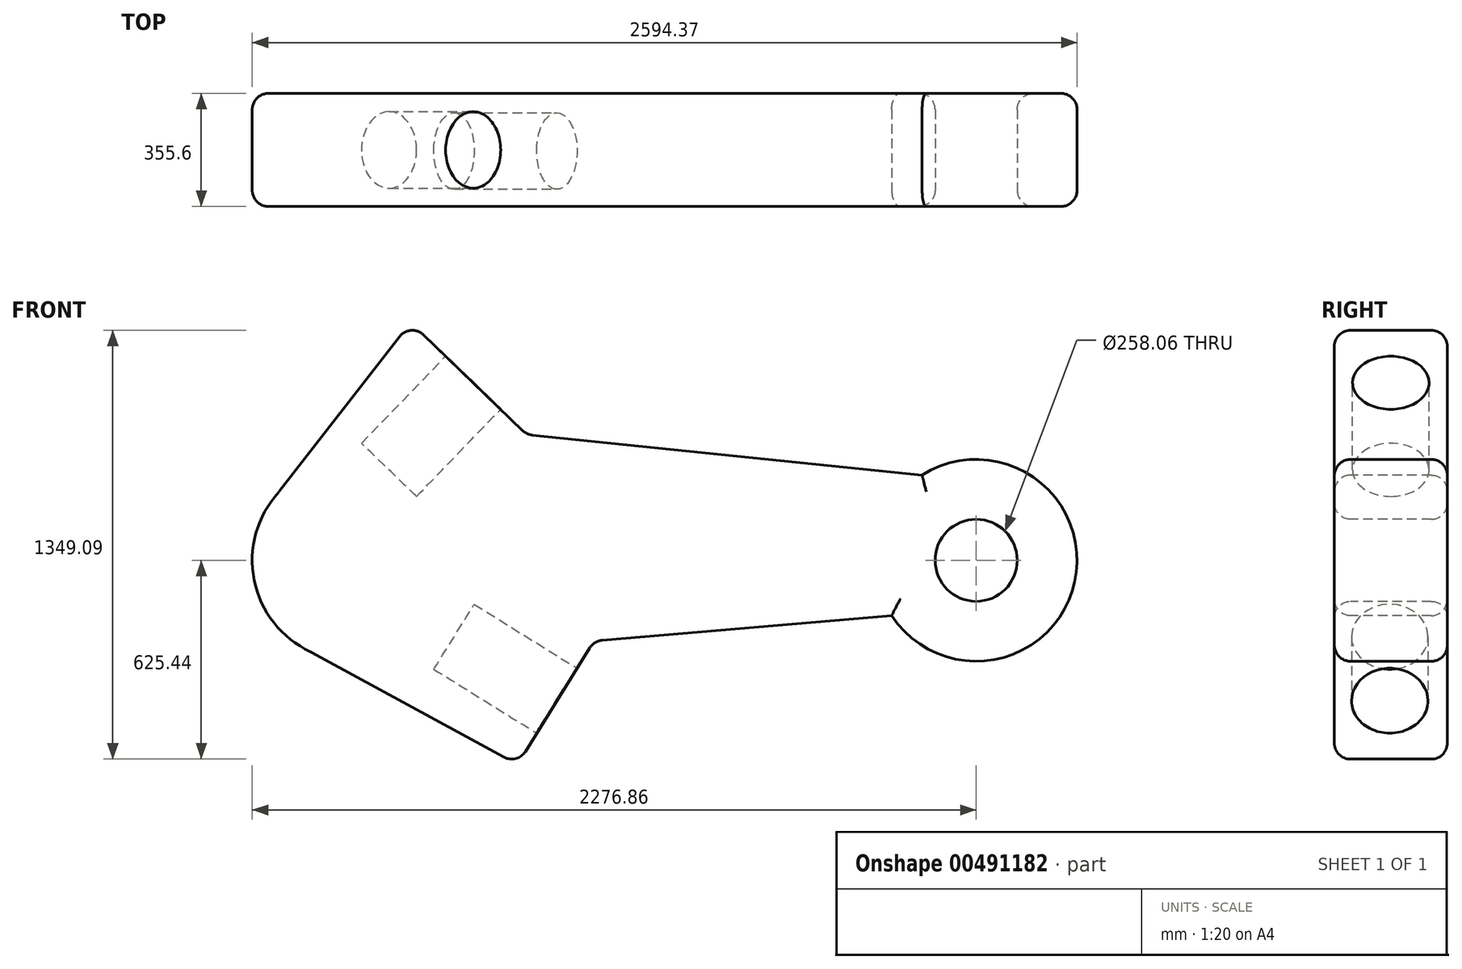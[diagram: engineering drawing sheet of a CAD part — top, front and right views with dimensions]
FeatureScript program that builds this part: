
annotation { "Feature Type Name" : "Feature", "Feature Type Description" : "" }
export const myFeature = defineFeature(function(context is Context, id is Id, definition is map)
    precondition{}
    {
        {
            var Q0;
            Q0=qCreatedBy(makeId("Front.planeOp"),FACE);
            var sketch = newSketch(context, id + "F0", { "sketchPlane" : qUnion([Q0])});
            skCircle(sketch, "E0", {"center": v(0, 0) * mm, "radius": 317.5 * mm});
            skLineSegment(sketch, "E1", {"start": v(317.5, 0) * mm, "end": v(757.44, -254) * mm});
            skLineSegment(sketch, "E2", {"start": v(757.44, -254) * mm, "end": v(515.93, -642.2) * mm});
            skLineSegment(sketch, "E3", {"start": v(180.55, 748.7) * mm, "end": v(546.1, 395.95) * mm});
            skLineSegment(sketch, "E4", {"start": v(546.1, 395.95) * mm, "end": v(317.5, 0) * mm});
            skLineSegment(sketch, "E5", {"start": v(180.55, 748.7) * mm, "end": v(-233.5, 215.14) * mm});
            skLineSegment(sketch, "E6", {"start": v(515.93, -642.2) * mm, "end": v(-132.66, -288.46) * mm});
            skLineSegment(sketch, "E7", {"start": v(546.1, 395.95) * mm, "end": v(496.6, 0) * mm});
            skLineSegment(sketch, "E8", {"start": v(496.6, 0) * mm, "end": v(757.44, -254) * mm});
            skCircle(sketch, "E9", {"center": v(1959.37, 0) * mm, "radius": 317.5 * mm});
            skLineSegment(sketch, "E10", {"start": v(546.1, 395.95) * mm, "end": v(1789.38, 268.17) * mm});
            skLineSegment(sketch, "E11", {"start": v(757.44, -254) * mm, "end": v(1693.84, -174.07) * mm});
            skCircle(sketch, "E12", {"center": v(1959.37, 0) * mm, "radius": 129.03 * mm});
            skSolve(sketch);
        }
        {
            var Q0;
            {var subQ4=sQuery(id+"F0.wireOp",EDGE,"E3");Q0=makeQuery(id+"F0.imprint","IMPRINT",FACE,{"disambiguationData":[TD([[makeQuery(id+"F0.imprint","IMPRINT",EDGE,{"derivedFrom":subQ4}),-1.0]])]});}
            var Q1;
            {var subQ0=sQuery(id+"F0.wireOp",EDGE,"E0");var subQ5=makeQuery(id+"F0.imprint","INTERSECT",VERTEX,{"derivedFrom":[subQ0,sQuery(id+"F0.wireOp",EDGE,"LNQtuhXF-bBcB-fDnA-nJkR-ZhhkIm1x3lj7")]});Q1=makeQuery(id+"F0.imprint","IMPRINT",FACE,{"disambiguationData":[TD([[makeQuery(id+"F0.imprint","IMPRINT",EDGE,{"disambiguationData":[TD([[subQ5,1.0]])],"derivedFrom":subQ0}),1.0]])]});}
            var Q2;
            {var subQ0=sQuery(id+"F0.wireOp",EDGE,"E1");Q2=makeQuery(id+"F0.imprint","IMPRINT",FACE,{"disambiguationData":[TD([[makeQuery(id+"F0.imprint","IMPRINT",EDGE,{"derivedFrom":subQ0}),-1.0]])]});}
            var Q3;
            Q3=makeQuery(id+"F0.imprint","IMPRINT",FACE,{"disambiguationData":[TD([[makeQuery(id+"F0.imprint","IMPRINT",EDGE,{"derivedFrom":sQuery(id+"F0.wireOp",EDGE,"E1")}),1.0]])]});
            var Q4;
            Q4=makeQuery(id+"F0.imprint","IMPRINT",FACE,{"disambiguationData":[TD([[makeQuery(id+"F0.imprint","IMPRINT",EDGE,{"derivedFrom":sQuery(id+"F0.wireOp",EDGE,"E7")}),1.0]])]});
            var Q5;
            Q5=makeQuery(id+"F0.imprint","IMPRINT",FACE,{"disambiguationData":[TD([[makeQuery(id+"F0.imprint","IMPRINT",EDGE,{"derivedFrom":sQuery(id+"F0.wireOp",EDGE,"E12")}),-1.0]])]});
            extrude(context, id + "F1", {"entities" : qUnion([Q0, Q1, Q2, Q3, Q4, Q5]), "oppositeDirection" : true, "depth" : 355.6 * mm, "offsetDistance" : 25.4 * mm});
        }
        {
            var Q0;
            Q0=makeQuery(id+"F1.opExtrude","SWEPT_FACE",FACE,{"disambiguationData":[OSD([sQuery(id+"F0.wireOp",EDGE,"E4")])]});
            var Q1;
            Q1=makeQuery(id+"F1.opExtrude","SWEPT_FACE",FACE,{"disambiguationData":[OSD([sQuery(id+"F0.wireOp",EDGE,"E3")])]});
            var Q2;
            Q2=makeQuery(id+"F1.opExtrude","CAP_FACE",FACE,{"disambiguationData":[OSD([sQuery(id+"F0.wireOp",EDGE,"E0"),sQuery(id+"F0.wireOp",EDGE,"E1"),sQuery(id+"F0.wireOp",EDGE,"E2"),sQuery(id+"F0.wireOp",EDGE,"E3"),sQuery(id+"F0.wireOp",EDGE,"E4"),sQuery(id+"F0.wireOp",EDGE,"E5"),sQuery(id+"F0.wireOp",EDGE,"E6")])],"isStart":true});
            var Q3;
            Q3=makeQuery(id+"F1.opExtrude","SWEPT_FACE",FACE,{"disambiguationData":[OSD([sQuery(id+"F0.wireOp",EDGE,"E2")])]});
            var Q4;
            Q4=makeQuery(id+"F1.opExtrude","CAP_FACE",FACE,{"disambiguationData":[OSD([sQuery(id+"F0.wireOp",EDGE,"E0"),sQuery(id+"F0.wireOp",EDGE,"E1"),sQuery(id+"F0.wireOp",EDGE,"E2"),sQuery(id+"F0.wireOp",EDGE,"E3"),sQuery(id+"F0.wireOp",EDGE,"E4"),sQuery(id+"F0.wireOp",EDGE,"E5"),sQuery(id+"F0.wireOp",EDGE,"E6")])],"isStart":false});
            var Q5;
            Q5=makeQuery(id+"F1.opExtrude","SWEPT_EDGE",EDGE,{"disambiguationData":[OSD([sQuery(id+"F0.wireOp",EDGE,"E0"),sQuery(id+"F0.wireOp",EDGE,"E6")])]});
            var Q6;
            Q6=makeQuery(id+"F1.opExtrude","SWEPT_FACE",FACE,{"disambiguationData":[OSD([sQuery(id+"F0.wireOp",EDGE,"E0")])]});
            fillet(context, id + "F2", {"entities" : qUnion([Q0, Q1, Q2, Q3, Q4, Q5, Q6]), "radius" : 50.8 * mm, "tangentPropagation" : true, "allowEdgeOverflow" : false});
        }
        {
            var Q0;
            Q0=makeQuery(id+"F1.opExtrude","SWEPT_FACE",FACE,{"disambiguationData":[OSD([sQuery(id+"F0.wireOp",EDGE,"E3")])]});
            var sketch = newSketch(context, id + "F3", { "sketchPlane" : qUnion([Q0])});
            skCircle(sketch, "E13", {"center": v(-116.45, 177.54) * mm, "radius": 120.32 * mm});
            skPoint(sketch, "E13.centerSnap0", {"position": v(-116.45, 304.8) * mm});
            skSolve(sketch);
        }
        {
            var Q0;
            Q0=makeQuery(id+"F3.imprint","IMPRINT",FACE,{"disambiguationData":[TD([[makeQuery(id+"F3.imprint","IMPRINT",EDGE,{"derivedFrom":sQuery(id+"F3.wireOp",EDGE,"E13")}),1.0]])]});
            var Q1;
            Q1=sQuery(id+"F3.wireOp",EDGE,"E13");
            extrude(context, id + "F4", {"entities" : qUnion([Q0]), "operationType" : NewBodyOperationType.REMOVE, "surfaceEntities" : qUnion([Q1]), "oppositeDirection" : true, "depth" : 381 * mm});
        }
        {
            var Q0;
            Q0=makeQuery(id+"F1.opExtrude","SWEPT_FACE",FACE,{"disambiguationData":[OSD([sQuery(id+"F0.wireOp",EDGE,"E2")])]});
            var sketch = newSketch(context, id + "F5", { "sketchPlane" : qUnion([Q0])});
            skCircle(sketch, "E14", {"center": v(174.35, -36.61) * mm, "radius": 120.32 * mm});
            skSolve(sketch);
        }
        {
            var Q0;
            Q0=makeQuery(id+"F5.imprint","IMPRINT",FACE,{"disambiguationData":[TD([[makeQuery(id+"F5.imprint","IMPRINT",EDGE,{"derivedFrom":sQuery(id+"F5.wireOp",EDGE,"E14")}),1.0]])]});
            extrude(context, id + "F6", {"entities" : qUnion([Q0]), "operationType" : NewBodyOperationType.REMOVE, "oppositeDirection" : true, "depth" : 381 * mm, "offsetDistance" : 25.4 * mm});
        }
    });
